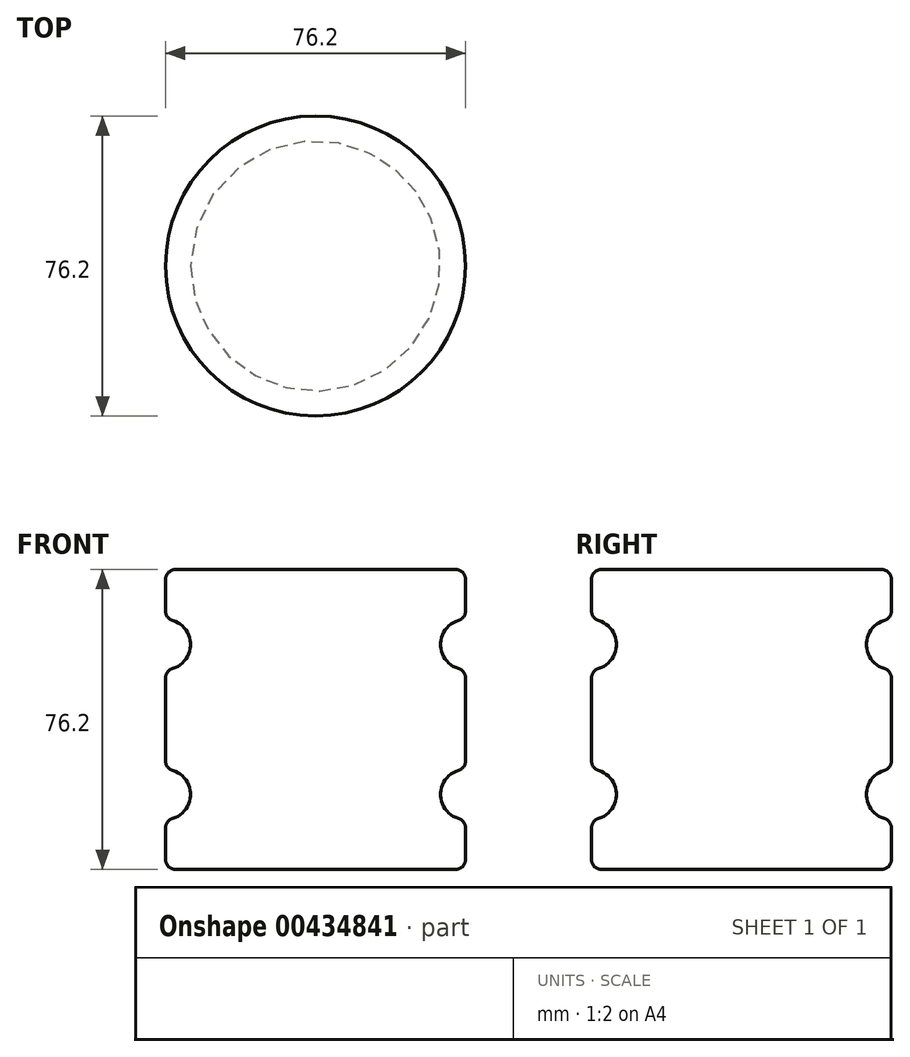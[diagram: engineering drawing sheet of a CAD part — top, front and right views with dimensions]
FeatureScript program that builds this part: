
annotation { "Feature Type Name" : "Feature", "Feature Type Description" : "" }
export const myFeature = defineFeature(function(context is Context, id is Id, definition is map)
    precondition{}
    {
        {
            var Q0;
            Q0=qCreatedBy(makeId("Front.planeOp"),FACE);
            var sketch = newSketch(context, id + "F0", { "sketchPlane" : qUnion([Q0])});
            skLineSegment(sketch, "E0.bottom", {"start": v(0, 0) * mm, "end": v(-38.1, 0) * mm});
            skLineSegment(sketch, "E0.top", {"start": v(0, 76.2) * mm, "end": v(-38.1, 76.2) * mm});
            skLineSegment(sketch, "E0.left", {"start": v(0, 0) * mm, "end": v(0, 76.2) * mm});
            skLineSegment(sketch, "E0.right", {"start": v(-38.1, 0) * mm, "end": v(-38.1, 76.2) * mm});
            skArc(sketch, "E1", {"start": v(0, 63.5) * mm, "mid": v(-6.35, 57.15) * mm, "end": v(0, 50.8) * mm});
            skArc(sketch, "E2", {"start": v(0, 25.4) * mm, "mid": v(-6.35, 19.05) * mm, "end": v(0, 12.7) * mm});
            skSolve(sketch);
        }
        {
            var Q0;
            {var subQ3=sQuery(id+"F0.wireOp",EDGE,"E0.bottom");Q0=makeQuery(id+"F0.imprint","IMPRINT",FACE,{"disambiguationData":[TD([[makeQuery(id+"F0.imprint","IMPRINT",EDGE,{"derivedFrom":subQ3}),-1.0]])]});}
            var Q1;
            Q1=sQuery(id+"F0.wireOp",EDGE,"E0.right");
            revolve(context, id + "F1", {"entities" : qUnion([Q0]), "axis" : qUnion([Q1]), "revolveType" : RevolveType.FULL});
        }
        {
            var Q0;
            Q0=makeQuery(id+"F1.opRevolve","SWEPT_EDGE",EDGE,{"disambiguationData":[OSD([sQuery(id+"F0.wireOp",EDGE,"E0.top"),sQuery(id+"F0.wireOp",EDGE,"E0.left")])]});
            var Q1;
            {var subQ0=sQuery(id+"F0.wireOp",EDGE,"E1");var subQ1=sQuery(id+"F0.wireOp",EDGE,"E0.left");Q1=makeQuery(id+"F1.opRevolve","SWEPT_EDGE",EDGE,{"disambiguationData":[OSD([subQ1,subQ0]),TDD([makeQuery(id+"F0.imprint","INTERSECT",VERTEX,{"disambiguationData":[OD(0.0)],"derivedFrom":[subQ1,subQ0]})])]});}
            var Q2;
            {var subQ0=sQuery(id+"F0.wireOp",EDGE,"E1");var subQ1=sQuery(id+"F0.wireOp",EDGE,"E0.left");Q2=makeQuery(id+"F1.opRevolve","SWEPT_EDGE",EDGE,{"disambiguationData":[OSD([subQ1,subQ0]),TDD([makeQuery(id+"F0.imprint","INTERSECT",VERTEX,{"disambiguationData":[OD(1.0)],"derivedFrom":[subQ1,subQ0]})])]});}
            var Q3;
            {var subQ0=sQuery(id+"F0.wireOp",EDGE,"E2");var subQ1=sQuery(id+"F0.wireOp",EDGE,"E0.left");Q3=makeQuery(id+"F1.opRevolve","SWEPT_EDGE",EDGE,{"disambiguationData":[OSD([subQ1,subQ0]),TDD([makeQuery(id+"F0.imprint","INTERSECT",VERTEX,{"disambiguationData":[OD(0.0)],"derivedFrom":[subQ1,subQ0]})])]});}
            var Q4;
            {var subQ0=sQuery(id+"F0.wireOp",EDGE,"E2");var subQ1=sQuery(id+"F0.wireOp",EDGE,"E0.left");Q4=makeQuery(id+"F1.opRevolve","SWEPT_EDGE",EDGE,{"disambiguationData":[OSD([subQ1,subQ0]),TDD([makeQuery(id+"F0.imprint","INTERSECT",VERTEX,{"disambiguationData":[OD(1.0)],"derivedFrom":[subQ1,subQ0]})])]});}
            var Q5;
            Q5=makeQuery(id+"F1.opRevolve","SWEPT_EDGE",EDGE,{"disambiguationData":[OSD([sQuery(id+"F0.wireOp",EDGE,"E0.bottom"),sQuery(id+"F0.wireOp",EDGE,"E0.left")])]});
            fillet(context, id + "F2", {"entities" : qUnion([Q0, Q1, Q2, Q3, Q4, Q5]), "radius" : 2.54 * mm, "tangentPropagation" : true, "allowEdgeOverflow" : false});
        }
    });
